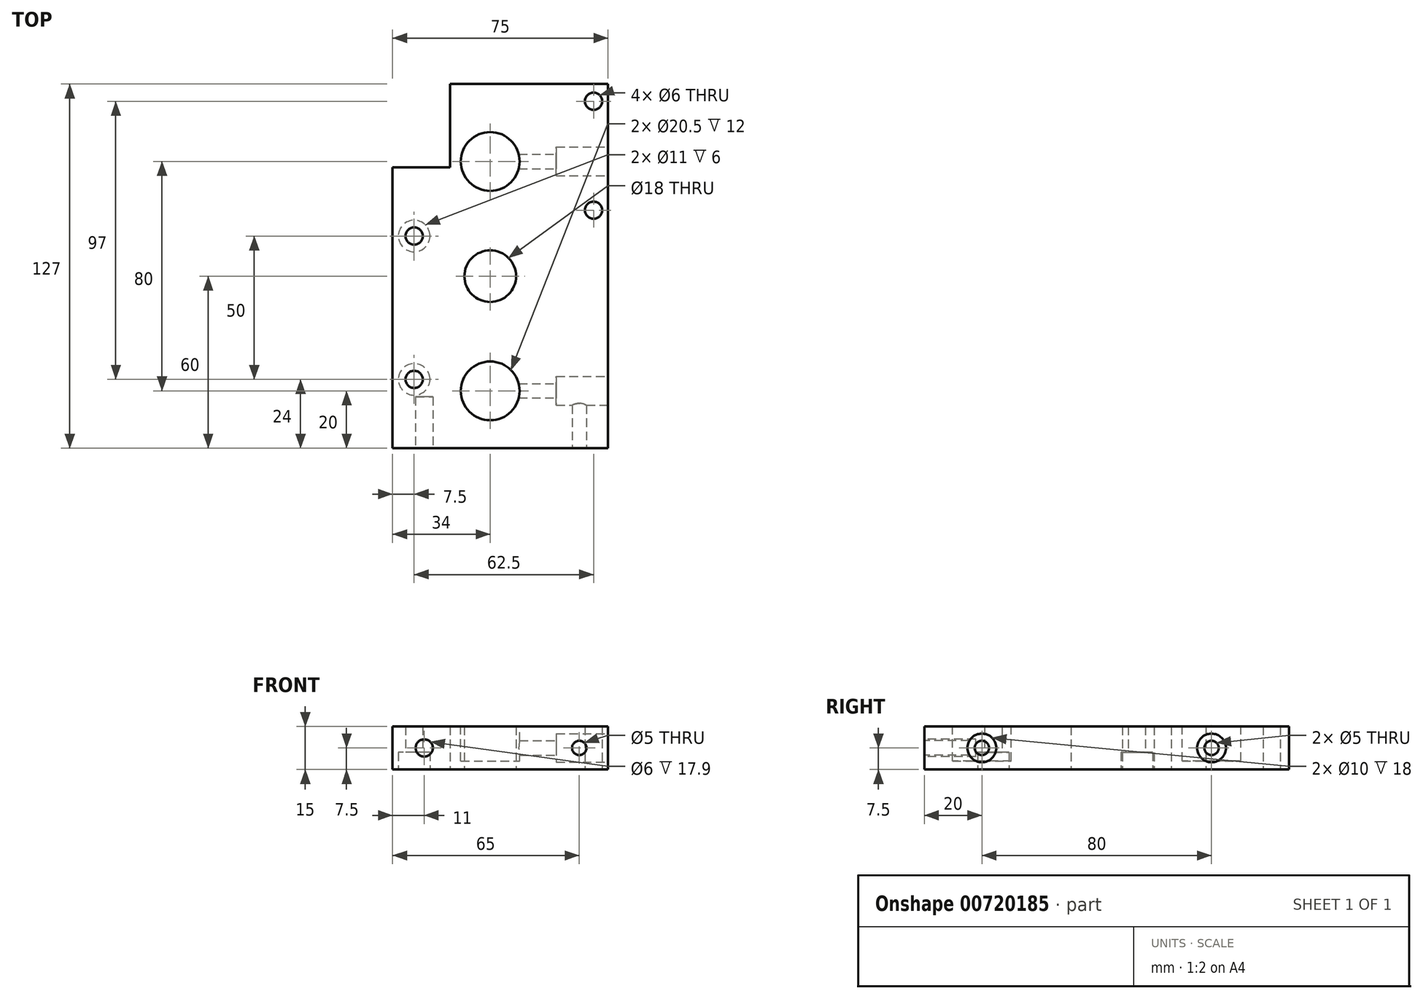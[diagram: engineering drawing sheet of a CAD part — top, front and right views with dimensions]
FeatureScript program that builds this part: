
annotation { "Feature Type Name" : "Feature", "Feature Type Description" : "" }
export const myFeature = defineFeature(function(context is Context, id is Id, definition is map)
    precondition{}
    {
        {
            var Q0;
            Q0=qCreatedBy(makeId("Top.planeOp"),FACE);
            var sketch = newSketch(context, id + "F0", { "sketchPlane" : qUnion([Q0])});
            skLineSegment(sketch, "E0.bottom", {"start": v(0, 0) * mm, "end": v(75, 0) * mm});
            skLineSegment(sketch, "E0.top", {"start": v(0, 127) * mm, "end": v(55, 127) * mm});
            skLineSegment(sketch, "E0.left", {"start": v(0, 0) * mm, "end": v(0, 127) * mm});
            skLineSegment(sketch, "E0.right", {"start": v(75, 0) * mm, "end": v(75, 98) * mm});
            skLineSegment(sketch, "E1.0", {"start": v(55, 98) * mm, "end": v(75, 98) * mm});
            skLineSegment(sketch, "E2.0", {"start": v(55, 98) * mm, "end": v(55, 127) * mm});
            skSolve(sketch);
        }
        {
            var Q0;
            Q0=qSketchRegion(id+"F0",true);
            extrude(context, id + "F1", {"entities" : qUnion([Q0]), "depth" : 15 * mm, "offsetDistance" : 25 * mm});
        }
        {
            var Q0;
            Q0=makeQuery(id+"F1.opExtrude","CAP_FACE",FACE,{"disambiguationData":[OSD([sQuery(id+"F0.wireOp",EDGE,"E0.bottom"),sQuery(id+"F0.wireOp",EDGE,"E0.top"),sQuery(id+"F0.wireOp",EDGE,"E0.left"),sQuery(id+"F0.wireOp",EDGE,"E0.right"),sQuery(id+"F0.wireOp",EDGE,"E1.0"),sQuery(id+"F0.wireOp",EDGE,"E2.0")])],"isStart":true});
            var sketch = newSketch(context, id + "F2", { "sketchPlane" : qUnion([Q0])});
            skCircle(sketch, "E3", {"center": v(5, -121) * mm, "radius": 3 * mm});
            skCircle(sketch, "E4", {"center": v(5, -83) * mm, "radius": 3 * mm});
            skCircle(sketch, "E5", {"center": v(41, -60) * mm, "radius": 9 * mm});
            skCircle(sketch, "E6", {"center": v(67.5, -24) * mm, "radius": 3 * mm});
            skCircle(sketch, "E7", {"center": v(67.5, -74) * mm, "radius": 3 * mm});
            skSolve(sketch);
        }
        {
            var Q0;
            Q0=qSketchRegion(id+"F2",true);
            extrude(context, id + "F3", {"entities" : qUnion([Q0]), "operationType" : NewBodyOperationType.REMOVE, "endBound" : BoundingType.THROUGH_ALL, "oppositeDirection" : true, "depth" : 25 * mm, "offsetDistance" : 25 * mm});
        }
        {
            var Q0;
            Q0=makeQuery(id+"F1.opExtrude","CAP_FACE",FACE,{"disambiguationData":[OSD([sQuery(id+"F0.wireOp",EDGE,"E0.bottom"),sQuery(id+"F0.wireOp",EDGE,"E0.top"),sQuery(id+"F0.wireOp",EDGE,"E0.left"),sQuery(id+"F0.wireOp",EDGE,"E0.right"),sQuery(id+"F0.wireOp",EDGE,"E1.0"),sQuery(id+"F0.wireOp",EDGE,"E2.0")])],"isStart":true});
            var sketch = newSketch(context, id + "F4", { "sketchPlane" : qUnion([Q0])});
            skCircle(sketch, "E8", {"center": v(67.5, -74) * mm, "radius": 5.5 * mm});
            skCircle(sketch, "E9", {"center": v(67.5, -24) * mm, "radius": 5.5 * mm});
            skSolve(sketch);
        }
        {
            var Q0;
            Q0=makeQuery(id+"F4.imprint","IMPRINT",FACE,{"disambiguationData":[TD([[makeQuery(id+"F4.imprint","IMPRINT",EDGE,{"derivedFrom":sQuery(id+"F4.wireOp",EDGE,"E8")}),1.0]])]});
            var Q1;
            Q1=makeQuery(id+"F4.imprint","IMPRINT",FACE,{"disambiguationData":[TD([[makeQuery(id+"F4.imprint","IMPRINT",EDGE,{"derivedFrom":sQuery(id+"F4.wireOp",EDGE,"E9")}),1.0]])]});
            extrude(context, id + "F5", {"entities" : qUnion([Q0, Q1]), "operationType" : NewBodyOperationType.REMOVE, "oppositeDirection" : true, "depth" : 6 * mm, "offsetDistance" : 25 * mm});
        }
        {
            var Q0;
            Q0=makeQuery(id+"F1.opExtrude","CAP_FACE",FACE,{"disambiguationData":[OSD([sQuery(id+"F0.wireOp",EDGE,"E0.bottom"),sQuery(id+"F0.wireOp",EDGE,"E0.top"),sQuery(id+"F0.wireOp",EDGE,"E0.left"),sQuery(id+"F0.wireOp",EDGE,"E0.right"),sQuery(id+"F0.wireOp",EDGE,"E1.0"),sQuery(id+"F0.wireOp",EDGE,"E2.0")])],"isStart":false});
            var sketch = newSketch(context, id + "F6", { "sketchPlane" : qUnion([Q0])});
            skCircle(sketch, "E10", {"center": v(41, 20) * mm, "radius": 10.25 * mm});
            skCircle(sketch, "E11", {"center": v(41, 100) * mm, "radius": 10.25 * mm});
            skSolve(sketch);
        }
        {
            var Q0;
            Q0=makeQuery(id+"F6.imprint","IMPRINT",FACE,{"disambiguationData":[TD([[makeQuery(id+"F6.imprint","IMPRINT",EDGE,{"derivedFrom":sQuery(id+"F6.wireOp",EDGE,"E11")}),1.0]])]});
            var Q1;
            Q1=makeQuery(id+"F6.imprint","IMPRINT",FACE,{"disambiguationData":[TD([[makeQuery(id+"F6.imprint","IMPRINT",EDGE,{"derivedFrom":sQuery(id+"F6.wireOp",EDGE,"E10")}),1.0]])]});
            extrude(context, id + "F7", {"entities" : qUnion([Q0, Q1]), "operationType" : NewBodyOperationType.REMOVE, "oppositeDirection" : true, "depth" : 12 * mm, "offsetDistance" : 25 * mm});
        }
        {
            var Q0;
            Q0=makeQuery(id+"F1.opExtrude","SWEPT_FACE",FACE,{"disambiguationData":[OSD([sQuery(id+"F0.wireOp",EDGE,"E0.left")])]});
            var sketch = newSketch(context, id + "F8", { "sketchPlane" : qUnion([Q0])});
            skCircle(sketch, "E12", {"center": v(-100, 7.5) * mm, "radius": 2.5 * mm});
            skPoint(sketch, "E12.centerSnap0", {"position": v(-127, 7.5) * mm});
            skCircle(sketch, "E13", {"center": v(-20, 7.5) * mm, "radius": 2.5 * mm});
            skSolve(sketch);
        }
        {
            var Q0;
            Q0=sQuery(id+"F8.wireOp",VERTEX,"E12.center");
            var Q1;
            Q1=sQuery(id+"F8.wireOp",VERTEX,"E13.center");
            var Q2;
            Q2=makeQuery(id+"F1.opExtrude","SWEPT_BODY",BODY,{"disambiguationData":[OSD([sQuery(id+"F0.wireOp",EDGE,"E0.bottom"),sQuery(id+"F0.wireOp",EDGE,"E0.top"),sQuery(id+"F0.wireOp",EDGE,"E0.left"),sQuery(id+"F0.wireOp",EDGE,"E0.right"),sQuery(id+"F0.wireOp",EDGE,"E1.0"),sQuery(id+"F0.wireOp",EDGE,"E2.0")])]});
            hole(context, id + "F9", {"style" : HoleStyle.SIMPLE, "endStyle" : HoleEndStyle.BLIND, "holeDiameter" : 5 * mm, "majorDiameter" : 5 * mm, "holeDepth" : 35 * mm, "isTappedThrough" : true, "tappedDepth" : 12 * mm, "tapClearance" : 3, "startFromSketch" : true, "locations" : qUnion([Q0, Q1]), "scope" : qUnion([Q2])});
        }
        {
            var Q0;
            Q0=makeQuery(id+"F1.opExtrude","SWEPT_FACE",FACE,{"disambiguationData":[OSD([sQuery(id+"F0.wireOp",EDGE,"E0.left")])]});
            var sketch = newSketch(context, id + "F10", { "sketchPlane" : qUnion([Q0])});
            skCircle(sketch, "E14", {"center": v(-100, 7.5) * mm, "radius": 5 * mm});
            skCircle(sketch, "E15", {"center": v(-20, 7.5) * mm, "radius": 5 * mm});
            skSolve(sketch);
        }
        {
            var Q0;
            Q0=makeQuery(id+"F10.imprint","IMPRINT",FACE,{"disambiguationData":[TD([[makeQuery(id+"F10.imprint","IMPRINT",EDGE,{"derivedFrom":sQuery(id+"F10.wireOp",EDGE,"E14")}),1.0]])]});
            var Q1;
            Q1=makeQuery(id+"F10.imprint","IMPRINT",FACE,{"disambiguationData":[TD([[makeQuery(id+"F10.imprint","IMPRINT",EDGE,{"derivedFrom":sQuery(id+"F10.wireOp",EDGE,"E15")}),1.0]])]});
            extrude(context, id + "F11", {"entities" : qUnion([Q0, Q1]), "operationType" : NewBodyOperationType.REMOVE, "oppositeDirection" : true, "depth" : 18 * mm, "offsetDistance" : 25 * mm});
        }
        {
            var Q0;
            Q0=makeQuery(id+"F1.opExtrude","SWEPT_FACE",FACE,{"disambiguationData":[OSD([sQuery(id+"F0.wireOp",EDGE,"E0.bottom")])]});
            var sketch = newSketch(context, id + "F12", { "sketchPlane" : qUnion([Q0])});
            skCircle(sketch, "E16", {"center": v(64, 7.5) * mm, "radius": 3 * mm});
            skPoint(sketch, "E16.centerSnap0", {"position": v(75, 7.5) * mm});
            skCircle(sketch, "E17", {"center": v(10, 7.5) * mm, "radius": 2.5 * mm});
            skSolve(sketch);
        }
        {
            var Q0;
            Q0=qSketchRegion(id+"F12",true);
            extrude(context, id + "F13", {"entities" : qUnion([Q0]), "operationType" : NewBodyOperationType.REMOVE, "oppositeDirection" : true, "depth" : 17.9 * mm, "offsetDistance" : 25 * mm});
        }
        {
            var Q0;
            Q0=makeQuery(id+"F1.opExtrude","SWEPT_BODY",BODY,{"disambiguationData":[OSD([sQuery(id+"F0.wireOp",EDGE,"E0.bottom"),sQuery(id+"F0.wireOp",EDGE,"E0.top"),sQuery(id+"F0.wireOp",EDGE,"E0.left"),sQuery(id+"F0.wireOp",EDGE,"E0.right"),sQuery(id+"F0.wireOp",EDGE,"E1.0"),sQuery(id+"F0.wireOp",EDGE,"E2.0")])]});
            var Q1;
            Q1=makeQuery(id+"F1.opExtrude","SWEPT_FACE",FACE,{"disambiguationData":[OSD([sQuery(id+"F0.wireOp",EDGE,"E0.left")])]});
            mirror(context, id + "F14", {"entities" : qUnion([Q0]), "mirrorPlane" : qUnion([Q1])});
        }
        {
            var Q0;
            Q0=makeQuery(id+"F1.opExtrude","SWEPT_BODY",BODY,{"disambiguationData":[OSD([sQuery(id+"F0.wireOp",EDGE,"E0.bottom"),sQuery(id+"F0.wireOp",EDGE,"E0.top"),sQuery(id+"F0.wireOp",EDGE,"E0.left"),sQuery(id+"F0.wireOp",EDGE,"E0.right"),sQuery(id+"F0.wireOp",EDGE,"E1.0"),sQuery(id+"F0.wireOp",EDGE,"E2.0")])]});
            deleteBodies(context, id + "F15", {"entities" : qUnion([Q0])});
        }
    });
